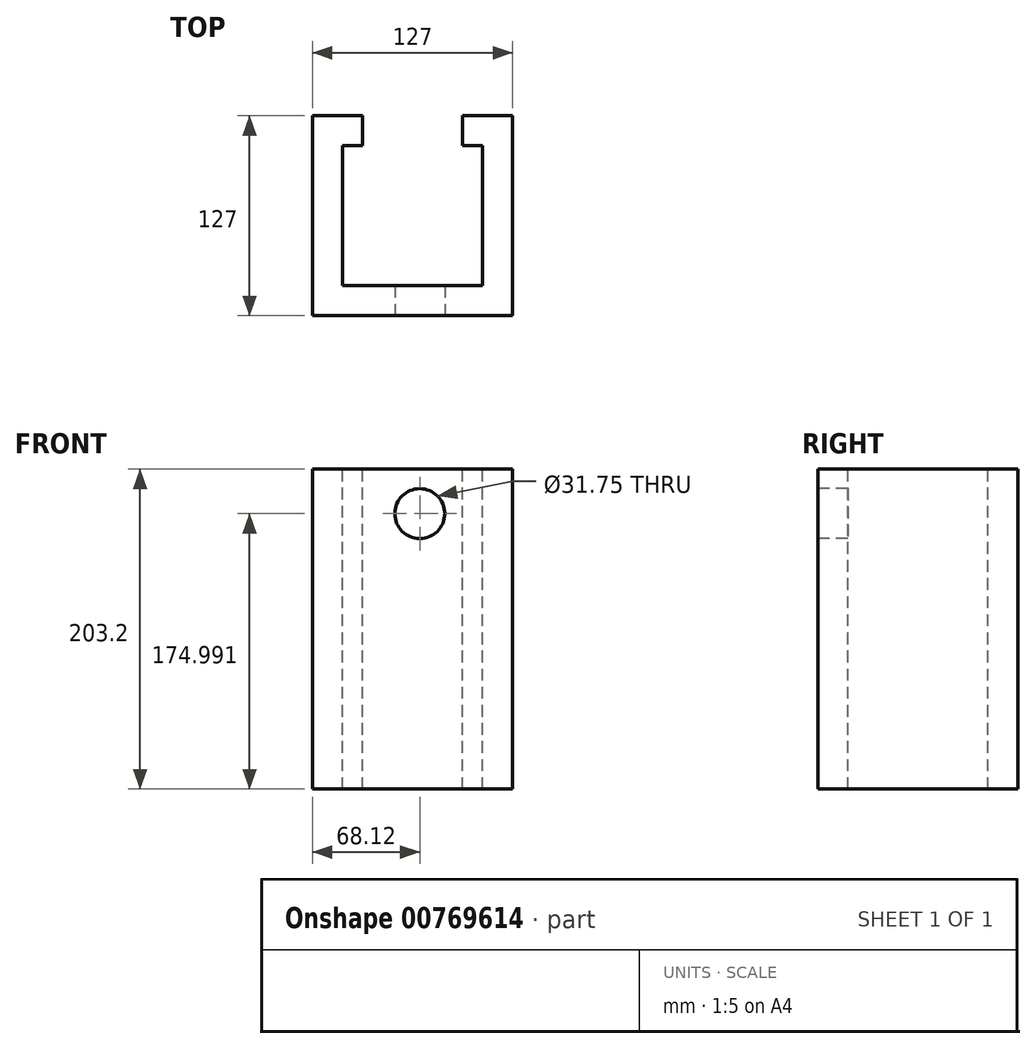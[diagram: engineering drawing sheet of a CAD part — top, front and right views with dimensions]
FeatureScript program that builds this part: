
annotation { "Feature Type Name" : "Feature", "Feature Type Description" : "" }
export const myFeature = defineFeature(function(context is Context, id is Id, definition is map)
    precondition{}
    {
        {
            var Q0;
            Q0=qCreatedBy(makeId("Front.planeOp"),FACE);
            var sketch = newSketch(context, id + "F0", { "sketchPlane" : qUnion([Q0])});
            skLineSegment(sketch, "E0.bottom", {"start": v(-68.12, 133.1) * mm, "end": v(58.88, 133.1) * mm});
            skLineSegment(sketch, "E0.top", {"start": v(-68.12, -70.1) * mm, "end": v(58.88, -70.1) * mm});
            skLineSegment(sketch, "E0.left", {"start": v(-68.12, 133.1) * mm, "end": v(-68.12, -70.1) * mm});
            skLineSegment(sketch, "E0.right", {"start": v(58.88, 133.1) * mm, "end": v(58.88, -70.1) * mm});
            skSolve(sketch);
        }
        {
            var Q0;
            Q0 = qSketchRegion(id + "F0", true);
            extrude(context, id + "F1", {"entities" : qUnion([Q0]), "depth" : 127 * mm, "offsetDistance" : 25.4 * mm});
        }
        {
            var Q0;
            Q0=makeQuery(id+"F1.opExtrude","SWEPT_FACE",FACE,{"disambiguationData":[OSD([sQuery(id+"F0.wireOp",EDGE,"E0.bottom")])]});
            var sketch = newSketch(context, id + "F2", { "sketchPlane" : qUnion([Q0])});
            skLineSegment(sketch, "E1.bottom", {"start": v(39.83, -107.95) * mm, "end": v(-49.07, -107.95) * mm});
            skLineSegment(sketch, "E1.right", {"start": v(-49.07, -107.95) * mm, "end": v(-49.07, -19.05) * mm});
            skLineSegment(sketch, "E2", {"start": v(-49.07, -19.05) * mm, "end": v(-36.37, -19.05) * mm});
            skLineSegment(sketch, "E3", {"start": v(-36.37, -19.05) * mm, "end": v(-36.37, 0) * mm});
            skLineSegment(sketch, "E4", {"start": v(-4.62, -107.95) * mm, "end": v(-4.62, 0) * mm, "construction": true});
            skLineSegment(sketch, "E5.MirrorCS", {"start": v(27.13, -19.05) * mm, "end": v(27.13, 0) * mm});
            skLineSegment(sketch, "E6.MirrorCS", {"start": v(39.83, -19.05) * mm, "end": v(27.13, -19.05) * mm});
            skLineSegment(sketch, "E7.MirrorCS", {"start": v(39.83, -107.95) * mm, "end": v(39.83, -19.05) * mm});
            skLineSegment(sketch, "E8", {"start": v(-36.37, 0) * mm, "end": v(27.13, 0) * mm});
            skSolve(sketch);
        }
        {
            var Q0;
            Q0 = qSketchRegion(id + "F2", true);
            extrude(context, id + "F3", {"entities" : qUnion([Q0]), "operationType" : NewBodyOperationType.REMOVE, "oppositeDirection" : true, "depth" : 203.2 * mm, "offsetDistance" : 25.4 * mm});
        }
        {
            var Q0;
            Q0=makeQuery(id+"F1.opExtrude","CAP_FACE",FACE,{"disambiguationData":[OSD([sQuery(id+"F0.wireOp",EDGE,"E0.bottom"),sQuery(id+"F0.wireOp",EDGE,"E0.top"),sQuery(id+"F0.wireOp",EDGE,"E0.left"),sQuery(id+"F0.wireOp",EDGE,"E0.right")])],"isStart":false});
            var sketch = newSketch(context, id + "F4", { "sketchPlane" : qUnion([Q0])});
            skCircle(sketch, "E9", {"center": v(0, 104.9) * mm, "radius": 15.88 * mm});
            skSolve(sketch);
        }
        {
            var Q0;
            Q0 = qSketchRegion(id + "F4", true);
            extrude(context, id + "F5", {"entities" : qUnion([Q0]), "operationType" : NewBodyOperationType.REMOVE, "oppositeDirection" : true, "depth" : 25.4 * mm, "offsetDistance" : 25.4 * mm});
        }
    });
